# Revit family: Shower-Bath_and_Shower_Trim-KOHLER-Coralais-K-T15201_1
name_source: partatom
category: Plumbing Fixtures
revit_build: Autodesk Revit 2015 (Build: 20140606_1530(x64)
units: mm (PartAtom-declared; Revit-internal decimal feet)

## types (2) — shared parameters
ADA Compliant = No
Assembly Code = D2010700
CW Connection = No
Cold Water Inlet = Cold Water Inlet
Date Modified = 12/19/2019
Default Elevation = 42"
Drain Included = No
Finish = Kohler-Metal-CP-Polished_Chrome
Flow Rate = 3 GPM
HW Connection = Yes
Handle Clearance = 3 1/16"
Height = 2 3/8"
Length = 6 5/16"
Manufacturer = KOHLER Co.
MasterFormat 1995 = 15410
MasterFormat 2004 = 22.41.23
Material = Brass Construction
Pressure = 80.00 psi
Product Documentation Link = https://www.us.kohler.com
Product Name = Coralais
Product Page URL = http://www.us.kohler.com
Tempered Water Inlet_1 = Tempered Water Inlet_1
Tempered Water Inlet_2 = Tempered Water Inlet_2
URL = https://www.us.kohler.com
Vent Connection = No
Waste Connection = No
Waste Water Outlet = Waste Water Outlet
WaterSense Certified = No

## per-type parameters (varying)
| type | Description | Model | Type |
| NPT Spout, CP- Polished Chrome | Bath/Shower trim set with lever handles, valve not included | K-T15201-4 | 1 |
| Slip-fit Spout, CP- Polished Chrome | Bath/Shower trim set with lever handles and slip-fit spout, valve not included | K-T15201-4S | 2 |

## geometry (parser evidence)
native form markers: Sweep x10
no freeform markers — native parametric forms only
